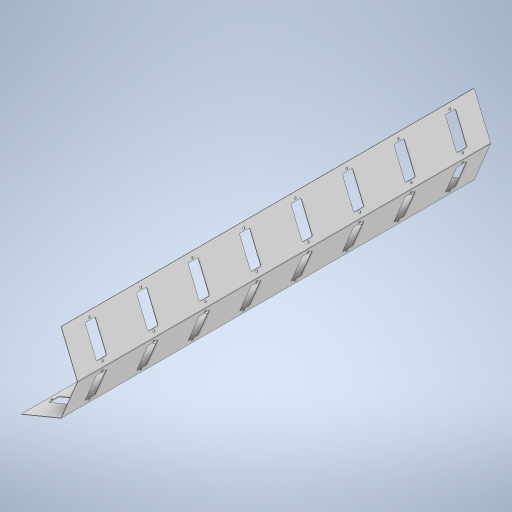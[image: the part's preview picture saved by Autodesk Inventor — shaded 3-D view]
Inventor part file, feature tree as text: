
AUTODESK INVENTOR PART (.ipt)
format: ipt  version: 2024.2 (Build 282272000, 272)  size: 739,840 bytes
history: native  units: mm
features: sheet_metal_op x3, other x3, sketch x2, extrude x1, fillet x1, pattern_circular x1, pattern_linear x1
ambient origin geometry x8: Origin, YZ Plane, XZ Plane, XY Plane, X Axis, Y Axis, Z Axis, Center Point
bodies: Body1 (feature_tree)
feature tree (12):
  sheet_metal_op  "Contour Flange2"
  extrude  "Extrusion4"  Depth=2.0mm
  fillet  "Fillet1"  Radius=1.0mm
  pattern_circular  "Circular Pattern1"  [2 undecoded]
  pattern_linear  "Rectangular Pattern2"  Spacing1=2006.0mm  [1 undecoded]
  other  "Corner Chamfer1"
  sketch  "Sketch2"  dims[d25=2.0mm d26=2.0mm d27=1.0mm]
  other  "Plate2"
  sheet_metal_op  "Bend2"
  sheet_metal_op  "Corner2"
  sketch  "Sketch10"  dims[d28=4.0mm d29=2.0mm d30=2006.0mm d31=2.0mm d32=3.0mm d33=8.0mm d34=2.0mm d35=2.0mm d56=506.0mm d58=4.0mm d69=0.9mm d70=4.0mm d71=0.9mm d107=145.0mm d108=50.0mm d109=10.0mm d110=10.0mm d112=0.0mm d113=0.0mm d114=5.0mm d115=30.0mm d116=90.0deg d118=125.0mm d119=80.0mm d121=250.0mm d122=2.0mm d123=6.0mm d124=45.0deg]
  other  "Definition1"
note: 3 required parameter values undecoded (feature->parameter linkage not recoverable at this tier; creation-order binding heuristic only, values carry confidence <= 0.55)
